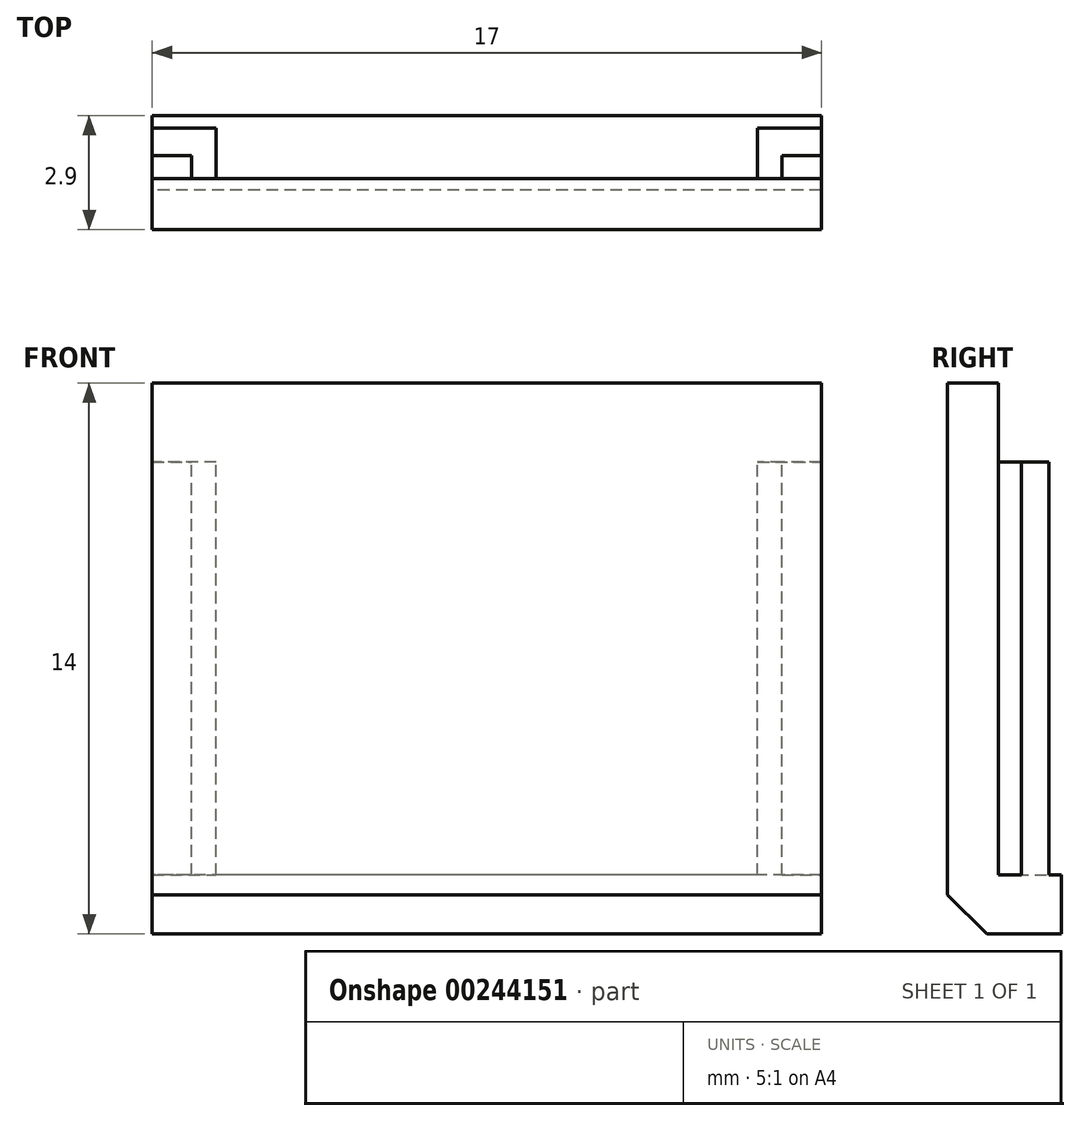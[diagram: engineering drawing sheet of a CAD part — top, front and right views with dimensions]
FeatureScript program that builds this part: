
annotation { "Feature Type Name" : "Feature", "Feature Type Description" : "" }
export const myFeature = defineFeature(function(context is Context, id is Id, definition is map)
    precondition{}
    {
        {
            var Q0;
            Q0=qCreatedBy(makeId("Top.planeOp"),FACE);
            var sketch = newSketch(context, id + "F0", { "sketchPlane" : qUnion([Q0])});
            skLineSegment(sketch, "E0", {"start": v(0, 0) * mm, "end": v(17, 0) * mm});
            skLineSegment(sketch, "E1", {"start": v(17, 0) * mm, "end": v(17, 2.9) * mm});
            skLineSegment(sketch, "E2", {"start": v(17, 2.9) * mm, "end": v(0, 2.9) * mm});
            skLineSegment(sketch, "E3", {"start": v(0, 2.9) * mm, "end": v(0, 0) * mm});
            skSolve(sketch);
        }
        {
            var Q0;
            Q0 = qSketchRegion(id + "F0", true);
            extrude(context, id + "F1", {"entities" : qUnion([Q0]), "depth" : 14 * mm});
        }
        {
            var Q0;
            Q0=makeQuery(id+"F1.opExtrude","CAP_FACE",FACE,{"disambiguationData":[OSD([sQuery(id+"F0.wireOp",EDGE,"E0"),sQuery(id+"F0.wireOp",EDGE,"E1"),sQuery(id+"F0.wireOp",EDGE,"E2"),sQuery(id+"F0.wireOp",EDGE,"E3")])],"isStart":false});
            var sketch = newSketch(context, id + "F2", { "sketchPlane" : qUnion([Q0])});
            skLineSegment(sketch, "E4", {"start": v(8.5, 2.9) * mm, "end": v(15.38, 2.9) * mm});
            skLineSegment(sketch, "E5", {"start": v(15.38, 2.9) * mm, "end": v(15.38, 1.3) * mm});
            skLineSegment(sketch, "E6", {"start": v(15.38, 1.3) * mm, "end": v(1.63, 1.3) * mm});
            skLineSegment(sketch, "E7", {"start": v(1.63, 1.3) * mm, "end": v(1.63, 2.9) * mm});
            skLineSegment(sketch, "E8", {"start": v(1.63, 2.9) * mm, "end": v(8.5, 2.9) * mm});
            skLineSegment(sketch, "E9", {"start": v(17, 0) * mm, "end": v(17, 1.3) * mm, "construction": true});
            skLineSegment(sketch, "E10", {"start": v(17, 1.3) * mm, "end": v(16, 1.3) * mm});
            skLineSegment(sketch, "E11", {"start": v(16, 1.3) * mm, "end": v(16, 1.88) * mm});
            skLineSegment(sketch, "E12", {"start": v(16, 1.88) * mm, "end": v(17, 1.88) * mm});
            skLineSegment(sketch, "E13", {"start": v(17, 1.88) * mm, "end": v(17, 1.3) * mm});
            skLineSegment(sketch, "E14", {"start": v(17, 1.88) * mm, "end": v(17, 2.58) * mm, "construction": true});
            skLineSegment(sketch, "E15", {"start": v(17, 2.58) * mm, "end": v(15.38, 2.58) * mm});
            skLineSegment(sketch, "E16", {"start": v(15.38, 2.9) * mm, "end": v(17, 2.9) * mm});
            skLineSegment(sketch, "E17", {"start": v(17, 2.9) * mm, "end": v(17, 2.58) * mm});
            skLineSegment(sketch, "E18", {"start": v(8.5, 2.9) * mm, "end": v(8.5, 0) * mm, "construction": true});
            skLineSegment(sketch, "E19.MirrorCS", {"start": v(0, 1.3) * mm, "end": v(1, 1.3) * mm});
            skLineSegment(sketch, "E20.MirrorCS", {"start": v(0, 1.88) * mm, "end": v(0, 1.3) * mm});
            skLineSegment(sketch, "E21.MirrorCS", {"start": v(1, 1.88) * mm, "end": v(0, 1.88) * mm});
            skLineSegment(sketch, "E22.MirrorCS", {"start": v(1, 1.3) * mm, "end": v(1, 1.88) * mm});
            skLineSegment(sketch, "E23.MirrorCS", {"start": v(1.63, 2.9) * mm, "end": v(0, 2.9) * mm});
            skLineSegment(sketch, "E24.MirrorCS", {"start": v(0, 2.58) * mm, "end": v(1.62, 2.58) * mm});
            skLineSegment(sketch, "E25.MirrorCS", {"start": v(0, 2.9) * mm, "end": v(0, 2.58) * mm});
            skSolve(sketch);
        }
        {
            var Q0;
            Q0 = qSketchRegion(id + "F2", true);
            extrude(context, id + "F3", {"entities" : qUnion([Q0]), "operationType" : NewBodyOperationType.REMOVE, "oppositeDirection" : true, "depth" : 12.5 * mm});
        }
        {
            var Q0;
            Q0=makeQuery(id+"F1.opExtrude","CAP_FACE",FACE,{"disambiguationData":[OSD([sQuery(id+"F0.wireOp",EDGE,"E0"),sQuery(id+"F0.wireOp",EDGE,"E1"),sQuery(id+"F0.wireOp",EDGE,"E2"),sQuery(id+"F0.wireOp",EDGE,"E3")])],"isStart":false});
            var sketch = newSketch(context, id + "F4", { "sketchPlane" : qUnion([Q0])});
            skLineSegment(sketch, "E26", {"start": v(0, 1.3) * mm, "end": v(17, 1.3) * mm});
            skLineSegment(sketch, "E27.0", {"start": v(17, 2.9) * mm, "end": v(0, 2.9) * mm});
            skLineSegment(sketch, "E28", {"start": v(17, 1.3) * mm, "end": v(17, 2.9) * mm});
            skLineSegment(sketch, "E29", {"start": v(0, 2.9) * mm, "end": v(0, 1.3) * mm});
            skSolve(sketch);
        }
        {
            var Q0;
            Q0 = qSketchRegion(id + "F4", true);
            extrude(context, id + "F5", {"entities" : qUnion([Q0]), "operationType" : NewBodyOperationType.REMOVE, "oppositeDirection" : true, "depth" : 2 * mm});
        }
        {
            var Q0;
            Q0=makeQuery(id+"F1.opExtrude","CAP_EDGE",EDGE,{"disambiguationData":[OSD([sQuery(id+"F0.wireOp",EDGE,"E0")])],"isStart":true});
            chamfer(context, id + "F6", {"entities" : qUnion([Q0]), "width" : 1 * mm, "tangentPropagation" : true});
        }
    });
